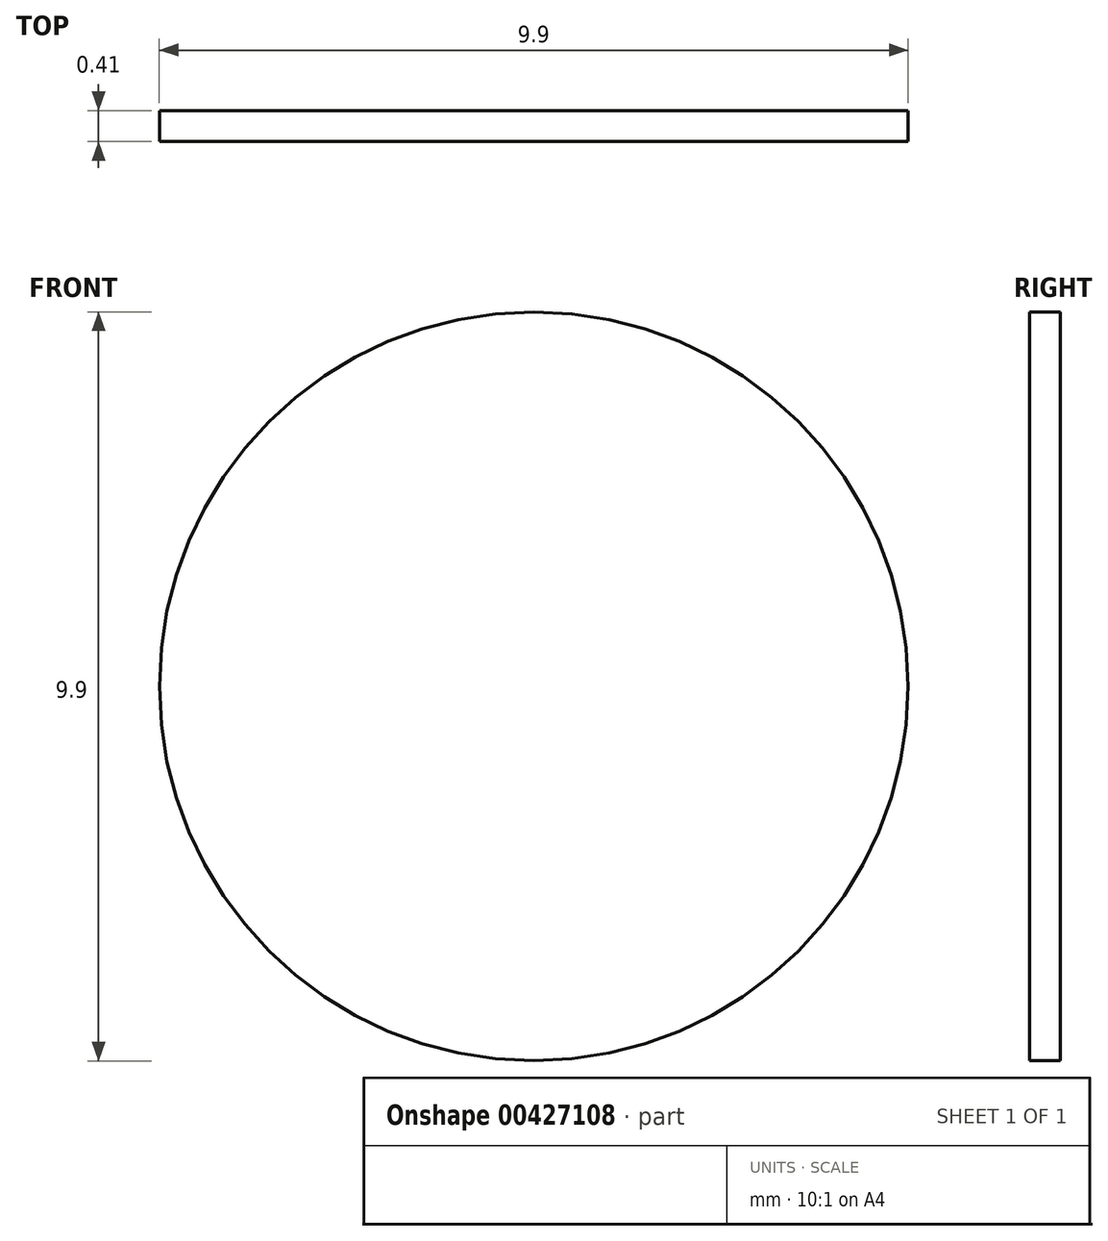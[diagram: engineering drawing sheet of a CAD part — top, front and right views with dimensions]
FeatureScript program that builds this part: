
annotation { "Feature Type Name" : "Feature", "Feature Type Description" : "" }
export const myFeature = defineFeature(function(context is Context, id is Id, definition is map)
    precondition{}
    {
        {
            var Q0;
            Q0=qCreatedBy(makeId("Front.planeOp"),FACE);
            var sketch = newSketch(context, id + "F0", { "sketchPlane" : qUnion([Q0])});
            skCircle(sketch, "E0", {"center": v(18.88, 40.6) * mm, "radius": 4.95 * mm});
            skSolve(sketch);
        }
        {
            var Q0;
            Q0=makeQuery(id+"F0.imprint","IMPRINT",FACE,{"disambiguationData":[TD([[makeQuery(id+"F0.imprint","IMPRINT",EDGE,{"derivedFrom":sQuery(id+"F0.wireOp",EDGE,"E0")}),1.0]])]});
            extrude(context, id + "F1", {"entities" : qUnion([Q0]), "depth" : 0.4 * mm});
        }
    });
